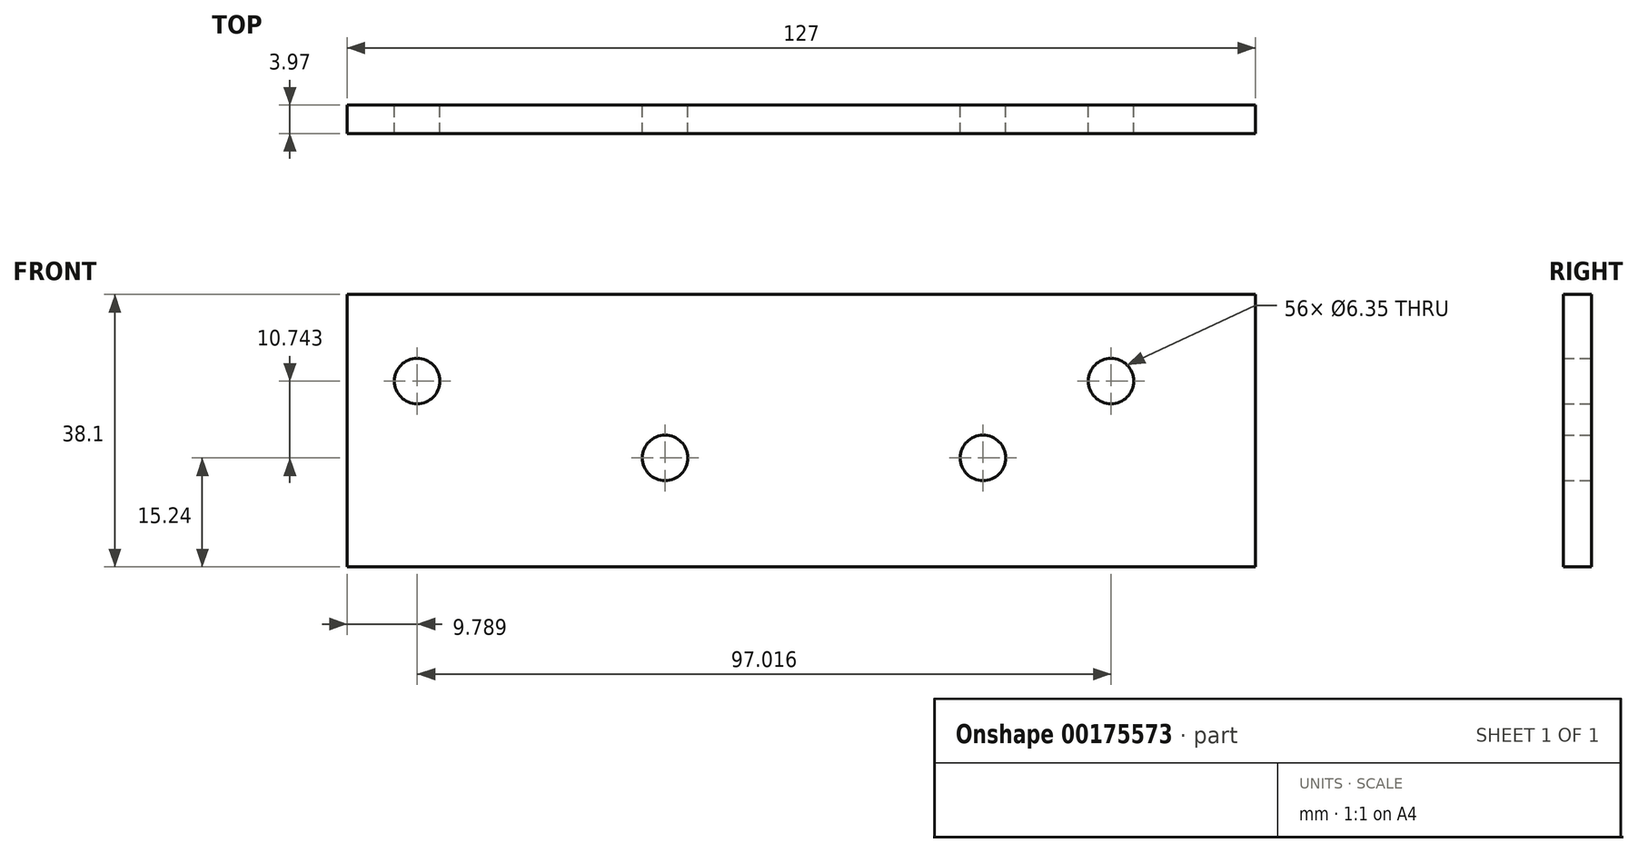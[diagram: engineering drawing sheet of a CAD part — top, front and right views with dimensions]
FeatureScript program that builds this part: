
annotation { "Feature Type Name" : "Feature", "Feature Type Description" : "" }
export const myFeature = defineFeature(function(context is Context, id is Id, definition is map)
    precondition{}
    {
        {
            var Q0;
            Q0=qCreatedBy(makeId("Front.planeOp"),FACE);
            var sketch = newSketch(context, id + "F0", { "sketchPlane" : qUnion([Q0])});
            skLineSegment(sketch, "E0.bottom", {"start": v(63.5, 19.05) * mm, "end": v(-63.5, 19.05) * mm});
            skLineSegment(sketch, "E0.top", {"start": v(63.5, -19.05) * mm, "end": v(-63.5, -19.05) * mm});
            skLineSegment(sketch, "E0.left", {"start": v(63.5, 19.05) * mm, "end": v(63.5, -19.05) * mm});
            skLineSegment(sketch, "E0.right", {"start": v(-63.5, 19.05) * mm, "end": v(-63.5, -19.05) * mm});
            skPoint(sketch, "E0.middle", {"position": v(0, 0) * mm});
            skLineSegment(sketch, "E1", {"start": v(0, -3.8) * mm, "end": v(25.4, -3.8) * mm});
            skLineSegment(sketch, "E2", {"start": v(0, -3.8) * mm, "end": v(-19.05, -3.8) * mm});
            skLineSegment(sketch, "E3", {"start": v(25.4, -3.8) * mm, "end": v(49.2, 22.62) * mm});
            skLineSegment(sketch, "E4", {"start": v(63.5, 19.05) * mm, "end": v(0, -19.05) * mm});
            skLineSegment(sketch, "E5", {"start": v(0, -19.05) * mm, "end": v(0, -9.52) * mm});
            skLineSegment(sketch, "E6", {"start": v(0, -9.52) * mm, "end": v(-53.71, 6.93) * mm});
            skLineSegment(sketch, "E7", {"start": v(0, -9.52) * mm, "end": v(10.5, -12.74) * mm});
            skCircle(sketch, "E8", {"center": v(-19.05, -3.81) * mm, "radius": 3.18 * mm});
            skCircle(sketch, "E9", {"center": v(25.4, -3.8) * mm, "radius": 3.18 * mm});
            skCircle(sketch, "E10", {"center": v(-53.71, 6.93) * mm, "radius": 3.18 * mm});
            skCircle(sketch, "E11", {"center": v(43.3, 6.93) * mm, "radius": 3.18 * mm});
            skSolve(sketch);
        }
        {
            var Q0;
            Q0=makeQuery(id+"F0.imprint","IMPRINT",FACE,{"disambiguationData":[TD([[makeQuery(id+"F0.imprint","IMPRINT",EDGE,{"derivedFrom":sQuery(id+"F0.wireOp",EDGE,"E0.bottom")}),1.0]])]});
            var Q1;
            {var subQ13=sQuery(id+"F0.wireOp",EDGE,"E0.right");Q1=makeQuery(id+"F0.imprint","IMPRINT",FACE,{"disambiguationData":[TD([[makeQuery(id+"F0.imprint","IMPRINT",EDGE,{"derivedFrom":subQ13}),1.0]])]});}
            var Q2;
            {var subQ4=sQuery(id+"F0.wireOp",EDGE,"E0.left");Q2=makeQuery(id+"F0.imprint","IMPRINT",FACE,{"disambiguationData":[TD([[makeQuery(id+"F0.imprint","IMPRINT",EDGE,{"derivedFrom":subQ4}),-1.0]])]});}
            var Q3;
            {var subQ0=sQuery(id+"F0.wireOp",EDGE,"E5");Q3=makeQuery(id+"F0.imprint","IMPRINT",FACE,{"disambiguationData":[TD([[makeQuery(id+"F0.imprint","IMPRINT",EDGE,{"derivedFrom":subQ0}),-1.0]])]});}
            var Q4;
            {var subQ0=sQuery(id+"F0.wireOp",EDGE,"E7");Q4=makeQuery(id+"F0.imprint","IMPRINT",FACE,{"disambiguationData":[TD([[makeQuery(id+"F0.imprint","IMPRINT",EDGE,{"derivedFrom":subQ0}),1.0]])]});}
            extrude(context, id + "F1", {"entities" : qUnion([Q0, Q1, Q2, Q3, Q4]), "depth" : 3.97 * mm});
        }
    });
